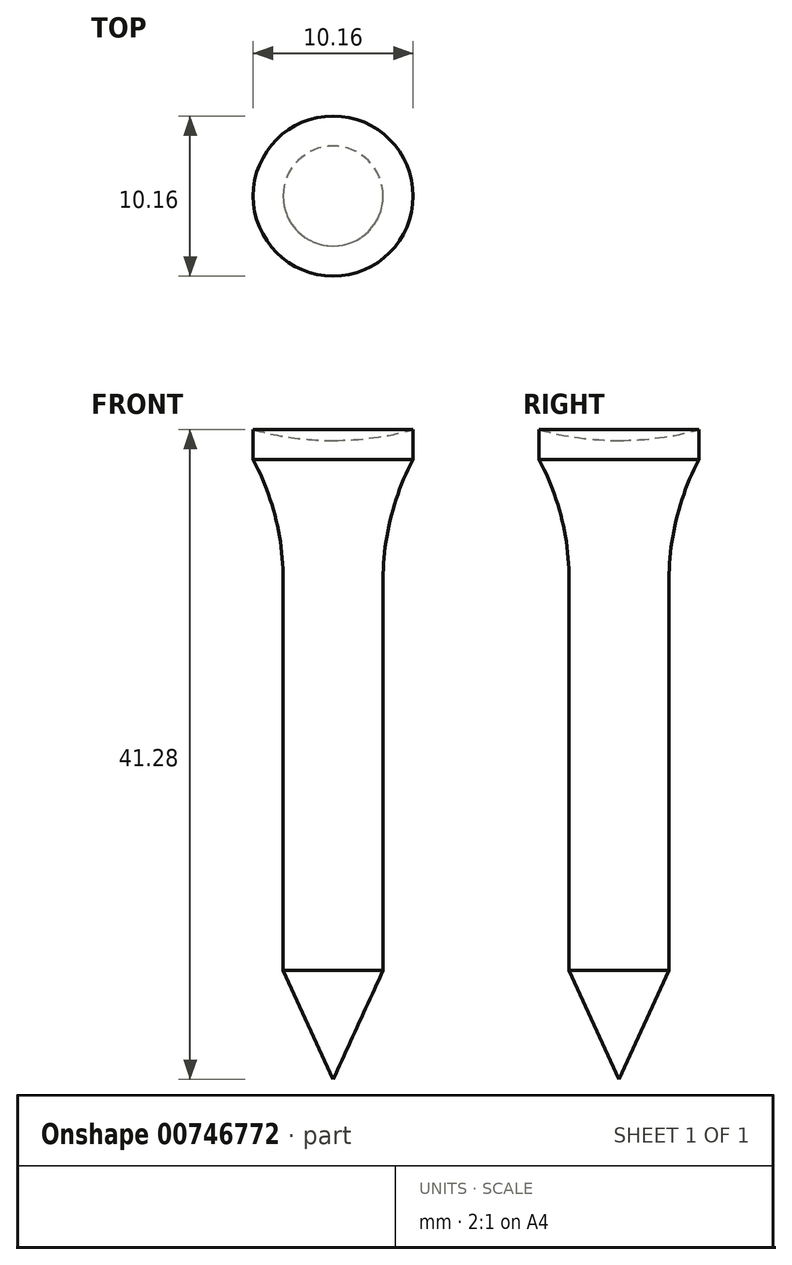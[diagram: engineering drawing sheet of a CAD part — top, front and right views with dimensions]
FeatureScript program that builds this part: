
annotation { "Feature Type Name" : "Feature", "Feature Type Description" : "" }
export const myFeature = defineFeature(function(context is Context, id is Id, definition is map)
    precondition{}
    {
        {
            var Q0;
            Q0=qCreatedBy(makeId("Front.planeOp"),FACE);
            var sketch = newSketch(context, id + "F0", { "sketchPlane" : qUnion([Q0])});
            skLineSegment(sketch, "E0", {"start": v(0, 0) * mm, "end": v(0, 31.75) * mm});
            skLineSegment(sketch, "E1", {"start": v(0, 31.75) * mm, "end": v(3.17, 31.75) * mm});
            skLineSegment(sketch, "E2", {"start": v(3.17, 31.75) * mm, "end": v(3.18, 6.93) * mm});
            skLineSegment(sketch, "E3", {"start": v(3.18, 6.93) * mm, "end": v(0, 0) * mm});
            skArc(sketch, "E4", {"start": v(5.08, 39.37) * mm, "mid": v(3.66, 35.68) * mm, "end": v(3.17, 31.75) * mm});
            skLineSegment(sketch, "E5", {"start": v(0, 31.75) * mm, "end": v(0, 39.37) * mm});
            skLineSegment(sketch, "E6", {"start": v(0, 39.37) * mm, "end": v(5.08, 39.37) * mm});
            skLineSegment(sketch, "E7", {"start": v(5.08, 39.37) * mm, "end": v(5.08, 41.27) * mm});
            skArc(sketch, "E8", {"start": v(0, 40.59) * mm, "mid": v(2.56, 40.76) * mm, "end": v(5.08, 41.27) * mm});
            skLineSegment(sketch, "E9", {"start": v(0, 39.37) * mm, "end": v(0, 40.59) * mm});
            skPoint(sketch, "E10.orphan", {"position": v(-5.08, 41.27) * mm});
            skSolve(sketch);
        }
        {
            var Q0;
            Q0 = qSketchRegion(id + "F0", true);
            var Q1;
            Q1=sQuery(id+"F0.wireOp",EDGE,"E9");
            revolve(context, id + "F1", {"surfaceOperationType" : NewSurfaceOperationType.NEW, "entities" : qUnion([Q0]), "axis" : qUnion([Q1]), "revolveType" : RevolveType.FULL});
        }
    });
